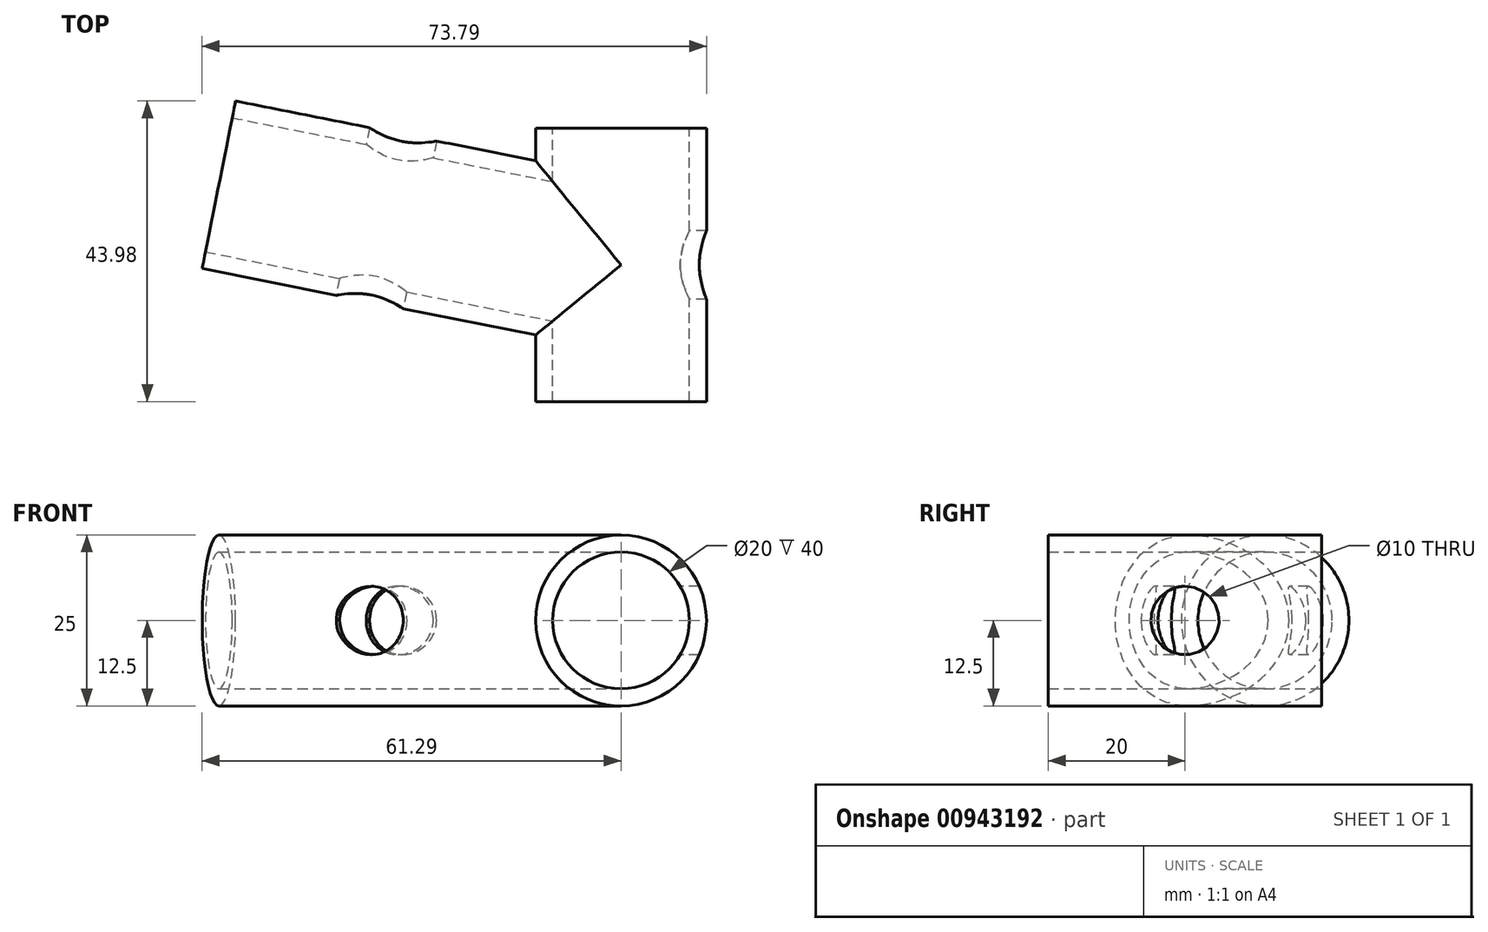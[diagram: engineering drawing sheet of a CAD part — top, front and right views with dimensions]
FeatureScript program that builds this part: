
annotation { "Feature Type Name" : "Feature", "Feature Type Description" : "" }
export const myFeature = defineFeature(function(context is Context, id is Id, definition is map)
    precondition{}
    {
        {
            var Q0;
            Q0=qCreatedBy(makeId("Front.planeOp"),FACE);
            var sketch = newSketch(context, id + "F0", { "sketchPlane" : qUnion([Q0])});
            skCircle(sketch, "E0", {"center": v(0, 0) * mm, "radius": 10 * mm});
            skCircle(sketch, "E1", {"center": v(0, 0) * mm, "radius": 12.5 * mm});
            skSolve(sketch);
        }
        {
            var Q0;
            Q0=makeQuery(id+"F0.imprint","IMPRINT",FACE,{"disambiguationData":[TD([[makeQuery(id+"F0.imprint","IMPRINT",EDGE,{"derivedFrom":sQuery(id+"F0.wireOp",EDGE,"E0")}),-1.0]])]});
            extrude(context, id + "F1", {"entities" : qUnion([Q0]), "depth" : 40 * mm, "offsetDistance" : 25 * mm, "symmetric" : true});
        }
        {
            var Q0;
            Q0=qCreatedBy(makeId("Right.planeOp"),FACE);
            var sketch = newSketch(context, id + "F2", { "sketchPlane" : qUnion([Q0])});
            skLineSegment(sketch, "E2", {"start": v(0, 0) * mm, "end": v(0, 40.77) * mm});
            skLineSegment(sketch, "E3", {"start": v(0, 40.77) * mm, "end": v(0, -49.46) * mm});
            skSolve(sketch);
        }
        {
            var Q0;
            Q0=qCreatedBy(makeId("Front.planeOp"),FACE);
            var Q1;
            Q1=sQuery(id+"F2.wireOp",EDGE,"E3");
            cPlane(context, id + "F3", {"entities" : qUnion([Q0, Q1]), "cplaneType" : CPlaneType.LINE_ANGLE, "offset" : 25 * mm, "angle" : 101.26 * degree, "width" : 150 * mm, "height" : 150 * mm});
        }
        {
            var Q0;
            Q0=qCreatedBy(id+"F3.planeOp",FACE);
            var sketch = newSketch(context, id + "F4", { "sketchPlane" : qUnion([Q0])});
            skCircle(sketch, "E4", {"center": v(0, 0) * mm, "radius": 10 * mm});
            skCircle(sketch, "E5", {"center": v(0, 0) * mm, "radius": 12.5 * mm});
            skSolve(sketch);
        }
        {
            var Q0;
            Q0=qSketchRegion(id+"F4",true);
            extrude(context, id + "F5", {"entities" : qUnion([Q0]), "operationType" : NewBodyOperationType.ADD, "oppositeDirection" : true, "depth" : 50 * mm, "offsetDistance" : 25 * mm});
        }
        {
            var Q0;
            Q0=qCreatedBy(makeId("Front.planeOp"),FACE);
            var sketch = newSketch(context, id + "F6", { "sketchPlane" : qUnion([Q0])});
            skCircle(sketch, "E6", {"center": v(0, 0) * mm, "radius": 10 * mm});
            skSolve(sketch);
        }
        {
            var Q0;
            Q0=qSketchRegion(id+"F6",true);
            extrude(context, id + "F7", {"entities" : qUnion([Q0]), "operationType" : NewBodyOperationType.REMOVE, "depth" : 50 * mm, "offsetDistance" : 25 * mm, "symmetric" : true});
        }
        {
            var Q0;
            Q0=qCreatedBy(id+"F3.planeOp",FACE);
            var sketch = newSketch(context, id + "F8", { "sketchPlane" : qUnion([Q0])});
            skCircle(sketch, "E7", {"center": v(0, 0) * mm, "radius": 10 * mm});
            skSolve(sketch);
        }
        {
            var Q0;
            Q0=qSketchRegion(id+"F8",true);
            extrude(context, id + "F9", {"entities" : qUnion([Q0]), "operationType" : NewBodyOperationType.REMOVE, "oppositeDirection" : true, "depth" : 25 * mm, "offsetDistance" : 25 * mm});
        }
        {
            var Q0;
            Q0=qCreatedBy(makeId("Right.planeOp"),FACE);
            var sketch = newSketch(context, id + "F10", { "sketchPlane" : qUnion([Q0])});
            skCircle(sketch, "E8", {"center": v(0, 0) * mm, "radius": 5 * mm});
            skSolve(sketch);
        }
        {
            var Q0;
            Q0=qSketchRegion(id+"F10",true);
            extrude(context, id + "F11", {"entities" : qUnion([Q0]), "operationType" : NewBodyOperationType.REMOVE, "depth" : 25 * mm, "offsetDistance" : 25 * mm});
        }
        {
            var Q0;
            Q0=sQuery(id+"F2.wireOp",EDGE,"E3");
            var Q1;
            Q1=qCreatedBy(id+"F3.planeOp",FACE);
            cPlane(context, id + "F12", {"entities" : qUnion([Q0, Q1]), "cplaneType" : CPlaneType.LINE_ANGLE, "offset" : 25 * mm, "angle" : 90 * degree, "width" : 150 * mm, "height" : 150 * mm});
        }
        {
            var Q0;
            Q0=qCreatedBy(id+"F12.planeOp",FACE);
            var sketch = newSketch(context, id + "F13", { "sketchPlane" : qUnion([Q0])});
            skCircle(sketch, "E9", {"center": v(35, 0) * mm, "radius": 5 * mm});
            skSolve(sketch);
        }
        {
            var Q0;
            Q0=qSketchRegion(id+"F13",true);
            extrude(context, id + "F14", {"entities" : qUnion([Q0]), "operationType" : NewBodyOperationType.REMOVE, "depth" : 30 * mm, "offsetDistance" : 25 * mm, "symmetric" : true});
        }
        {
            var Q0;
            Q0=makeQuery(id+"F5.opExtrude","CAP_FACE",FACE,{"disambiguationData":[OSD([sQuery(id+"F4.wireOp",EDGE,"E4"),sQuery(id+"F4.wireOp",EDGE,"E5")])],"isStart":false});
            extrude(context, id + "F15", {"entities" : qUnion([Q0]), "operationType" : NewBodyOperationType.ADD, "depth" : 10 * mm, "offsetDistance" : 25 * mm});
        }
    });
